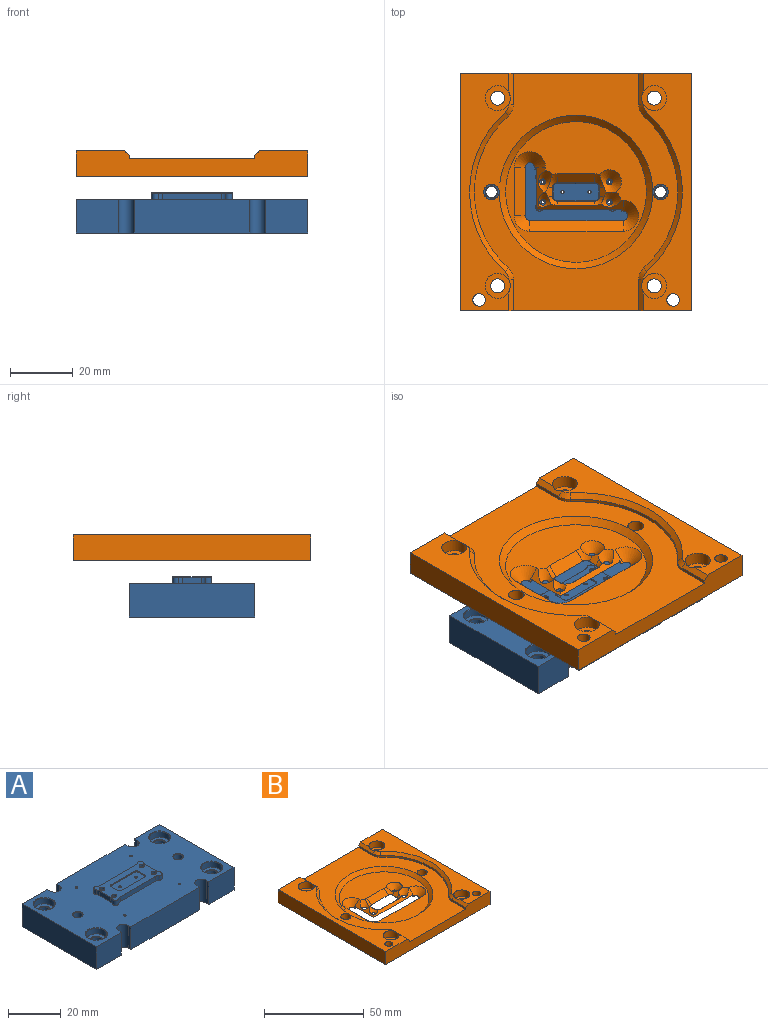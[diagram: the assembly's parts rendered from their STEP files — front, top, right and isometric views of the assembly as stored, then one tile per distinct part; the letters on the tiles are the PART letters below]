
ASSEMBLY  parts=2 mates=2
PART A: 211 faces, bbox 74x40x12.8 mm
  f0: plane 74x40mm, normal (0,0,-1), area 1926mm2, adj f20,f21,f22,f23,f24,f25,f26,f27
  f1: cylinder r=15mm len=15.84mm, axis (0,0,-1), area 30.9mm2, adj f61,f166,f171,f200
  f2: cylinder r=15mm len=15.14mm, axis (0,0,-1), area 29.4mm2, adj f61,f174,f175,f179
  f3: cylinder r=15mm len=18.2mm, axis (0,0,-1), area 36.2mm2, adj f61,f176,f177,f191
  f4: cylinder r=0.5mm len=1mm, axis (0,0,1), area 3.1mm2, adj f17,f158
  f5: cylinder r=0.5mm len=1mm, axis (0,0,1), area 3.1mm2, adj f16,f156
  f6: cylinder r=0.5mm len=1mm, axis (0,0,1), area 3.1mm2, adj f15,f154
  f7: cylinder r=0.5mm len=1mm, axis (0,0,1), area 3.1mm2, adj f14,f152
  f8: cylinder r=0.5mm len=1mm, axis (0,0,1), area 3.1mm2, adj f92,f150
  f9: cylinder r=0.5mm len=1mm, axis (0,0,1), area 3.1mm2, adj f92,f148
  f10: cylinder r=0.5mm len=1mm, axis (0,0,1), area 1.9mm2, adj f62,f145
  f11: cylinder r=0.5mm len=1mm, axis (0,0,1), area 1.9mm2, adj f62,f143
  f12: cylinder r=0.5mm len=1mm, axis (0,0,1), area 1.9mm2, adj f62,f141
  f13: cylinder r=0.5mm len=1mm, axis (0,0,1), area 1.9mm2, adj f62,f139
  f14: cone r=0mm half-angle=59deg, axis (0,0,1), area 2.7mm2, adj f7,f80
  f15: cone r=0mm half-angle=59deg, axis (0,0,1), area 2.7mm2, adj f6,f81
  f16: cone r=0mm half-angle=59deg, axis (0,0,1), area 2.7mm2, adj f5,f82
  f17: cone r=0mm half-angle=59deg, axis (0,0,1), area 2.7mm2, adj f4,f83
  f18: plane 25.7x12.2mm, normal (0,0,1), area 175.2mm2, adj f93,f94,f95,f96,f97,f98,f99,f100
  f19: cylinder r=0.3mm len=2.15mm, axis (0,0,1), area 0mm2, adj f62,f64,f77,f122
  f20: cylinder r=2.5mm len=10.6mm, axis (0,0,-1), area 83.3mm2, adj f0,f21,f44,f62
  f21: plane 10.6x1.5mm, normal (-1,0,0), area 15.9mm2, adj f0,f20,f22,f62
  f22: plane 13.5x10.6mm, normal (0,-1,0), area 143.1mm2, adj f0,f21,f23,f62
  f23: plane 40x10.6mm, normal (1,0,0), area 424mm2, adj f0,f22,f24,f62
  f24: plane 13.5x10.6mm, normal (0,1,0), area 143.1mm2, adj f0,f23,f25,f62
  f25: plane 10.6x1.5mm, normal (-1,0,0), area 15.9mm2, adj f0,f24,f26,f62
  f26: cylinder r=2.5mm len=10.6mm, axis (0,0,-1), area 83.3mm2, adj f0,f25,f27,f62
  f27: plane 10.6x1.5mm, normal (1,0,0), area 15.9mm2, adj f0,f26,f28,f62
  f28: plane 37x10.6mm, normal (0,1,0), area 392.2mm2, adj f0,f27,f29,f62
  f29: plane 10.6x1.5mm, normal (-1,0,0), area 15.9mm2, adj f0,f28,f30,f62
  f30: cylinder r=2.5mm len=10.6mm, axis (0,0,-1), area 83.3mm2, adj f0,f29,f31,f62
  f31: plane 10.6x1.5mm, normal (1,0,0), area 15.9mm2, adj f0,f30,f32,f62
  f32: plane 13.5x10.6mm, normal (0,1,0), area 143.1mm2, adj f0,f31,f33,f62
  f33: plane 40x10.6mm, normal (-1,0,0), area 424mm2, adj f0,f32,f34,f62
  f34: plane 13.5x10.6mm, normal (0,-1,0), area 143.1mm2, adj f0,f33,f35,f62
  f35: plane 10.6x1.5mm, normal (1,0,0), area 15.9mm2, adj f0,f34,f36,f62
  f36: cylinder r=2.5mm len=10.6mm, axis (0,0,-1), area 83.3mm2, adj f0,f35,f37,f62
  f37: plane 10.6x1.5mm, normal (-1,0,0), area 15.9mm2, adj f0,f36,f38,f62
  f38: plane 37x10.6mm, normal (0,-1,0), area 392.2mm2, adj f0,f37,f44,f62
  f39: cylinder r=4mm len=8mm, axis (0,0,-1), area 65.3mm2, adj f51,f135
  f40: cylinder r=1.8mm len=10.2mm, axis (0,0,-1), area 115.4mm2, adj f125,f134
  f41: cylinder r=1.8mm len=10.2mm, axis (0,0,-1), area 115.4mm2, adj f127,f133
  f42: cylinder r=4mm len=8mm, axis (0,0,-1), area 65.3mm2, adj f53,f136
  f43: cylinder r=4mm len=8mm, axis (0,0,-1), area 65.3mm2, adj f49,f138
  f44: plane 10.6x1.5mm, normal (1,0,0), area 15.9mm2, adj f0,f20,f38,f62
  f45: cylinder r=4mm len=8mm, axis (0,0,-1), area 65.3mm2, adj f47,f137
  f46: cylinder r=2.25mm len=7.4mm, axis (0,0,-1), area 104.6mm2, adj f126,f132
  f47: plane 8x8mm, normal (0,0,1), area 31.4mm2, adj f45,f132
  f48: cylinder r=2.25mm len=7.4mm, axis (0,0,-1), area 104.6mm2, adj f128,f131
  f49: plane 8x8mm, normal (0,0,1), area 31.4mm2, adj f43,f131
  f50: cylinder r=2.25mm len=7.4mm, axis (0,0,-1), area 104.6mm2, adj f124,f130
  f51: plane 8x8mm, normal (0,0,1), area 31.4mm2, adj f39,f130
  f52: cylinder r=2.25mm len=7.4mm, axis (0,0,-1), area 104.6mm2, adj f123,f129
  f53: plane 8x8mm, normal (0,0,1), area 31.4mm2, adj f42,f129
  f54: cone r=0mm half-angle=59deg, axis (0,0,-1), area 14.7mm2, adj f55
  f55: cylinder r=2mm len=4.85mm, axis (0,0,-1), area 60.9mm2, adj f54,f58
  f56: cone r=0mm half-angle=59deg, axis (0,0,-1), area 14.7mm2, adj f57
  f57: cylinder r=2mm len=4.85mm, axis (0,0,-1), area 60.9mm2, adj f56,f59
  f58: cone r=2mm half-angle=45deg, axis (0,0,-1), area 2.8mm2, adj f0,f55
  f59: cone r=2mm half-angle=45deg, axis (0,0,-1), area 2.8mm2, adj f0,f57
  f60: cylinder r=15mm len=18.2mm, axis (0,0,-1), area 36.2mm2, adj f61,f172,f173,f188
  f61: plane 33.6x30.2mm, normal (0,0,-1), area 728.5mm2, adj f1,f2,f3,f60,f159,f160,f161,f162
  f62: plane 74x40mm, normal (0,0,1), area 2368.6mm2, adj f10,f11,f12,f13,f19,f20,f21,f22
  f63: plane 6.04x2.15mm, normal (-1,0,0), area 13mm2, adj f62,f68,f73,f113
  f64: plane 19.05x2.15mm, normal (0,1,0), area 41mm2, adj f19,f62,f70,f121
  f65: plane 6.04x2.15mm, normal (1,0,0), area 13mm2, adj f62,f74,f79,f114
  f66: cylinder r=0.3mm len=2.15mm, axis (0,0,1), area 0mm2, adj f62,f67,f76,f106
  f67: plane 19.05x2.15mm, normal (0,-1,0), area 41mm2, adj f62,f66,f71,f105
  f68: cylinder r=2mm len=2.15mm, axis (0,0,1), area 2.7mm2, adj f62,f63,f69,f115
  f69: cylinder r=1.25mm len=2.15mm, axis (0,0,1), area 7.8mm2, adj f62,f68,f70,f117
  f70: cylinder r=2mm len=2.15mm, axis (0,0,1), area 3.1mm2, adj f62,f64,f69,f119
  f71: cylinder r=2mm len=2.15mm, axis (0,0,1), area 3.1mm2, adj f62,f67,f72,f107
  f72: cylinder r=1.25mm len=2.15mm, axis (0,0,1), area 7.8mm2, adj f62,f71,f73,f109
  f73: cylinder r=2mm len=2.15mm, axis (0,0,1), area 2.7mm2, adj f62,f63,f72,f111
  f74: cylinder r=2mm len=2.15mm, axis (0,0,1), area 2.7mm2, adj f62,f65,f75,f112
  f75: cylinder r=1.25mm len=2.15mm, axis (0,0,1), area 7.8mm2, adj f62,f74,f76,f110
  f76: cylinder r=2mm len=2.15mm, axis (0,0,1), area 3mm2, adj f62,f66,f75,f108
  f77: cylinder r=2mm len=2.15mm, axis (0,0,1), area 3mm2, adj f19,f62,f78,f120
  f78: cylinder r=1.25mm len=2.15mm, axis (0,0,1), area 7.8mm2, adj f62,f77,f79,f118
  f79: cylinder r=2mm len=2.15mm, axis (0,0,1), area 2.7mm2, adj f62,f65,f78,f116
  f80: cylinder r=1mm len=2mm, axis (0,0,1), area 6mm2, adj f14,f104
  f81: cylinder r=1mm len=2mm, axis (0,0,1), area 6mm2, adj f15,f103
  f82: cylinder r=1mm len=2mm, axis (0,0,1), area 6mm2, adj f16,f102
  f83: cylinder r=1mm len=2mm, axis (0,0,1), area 6mm2, adj f17,f101
  f84: plane 3.43x0.45mm, normal (-1,0,0), area 1.5mm2, adj f85,f91,f92,f95
  f85: cylinder r=1mm len=1mm, axis (0,0,1), area 0.7mm2, adj f84,f86,f92,f93
  f86: plane 12.43x0.45mm, normal (0,-1,0), area 5.6mm2, adj f85,f87,f92,f94
  f87: cylinder r=1mm len=1mm, axis (0,0,1), area 0.7mm2, adj f86,f88,f92,f96
  f88: plane 3.43x0.45mm, normal (1,0,0), area 1.5mm2, adj f87,f89,f92,f98
  f89: cylinder r=1mm len=1mm, axis (0,0,1), area 0.7mm2, adj f88,f90,f92,f100
  f90: plane 12.43x0.45mm, normal (0,1,0), area 5.6mm2, adj f89,f91,f92,f99
  f91: cylinder r=1mm len=1mm, axis (0,0,1), area 0.7mm2, adj f84,f90,f92,f97
  f92: plane 14.43x5.43mm, normal (0,0,1), area 75.8mm2, adj f8,f9,f84,f85,f86,f87,f88,f89
  f93: cone r=1mm half-angle=45deg, axis (0,0,1), area 0.1mm2, adj f18,f85,f94,f95
  f94: plane 12.43x0.05mm, normal (0,-0.71,0.71), area 0.9mm2, adj f18,f86,f93,f96
  f95: plane 3.43x0.05mm, normal (-0.71,0,0.71), area 0.2mm2, adj f18,f84,f93,f97
  f96: cone r=1mm half-angle=45deg, axis (0,0,1), area 0.1mm2, adj f18,f87,f94,f98
  f97: cone r=1mm half-angle=45deg, axis (0,0,1), area 0.1mm2, adj f18,f91,f95,f99
  f98: plane 3.43x0.05mm, normal (0.71,0,0.71), area 0.2mm2, adj f18,f88,f96,f100
  f99: plane 12.43x0.05mm, normal (0,0.71,0.71), area 0.9mm2, adj f18,f90,f97,f100
  f100: cone r=1mm half-angle=45deg, axis (0,0,1), area 0.1mm2, adj f18,f89,f98,f99
  f101: cone r=1mm half-angle=45deg, axis (0,0,1), area 0.5mm2, adj f18,f83
  f102: cone r=1mm half-angle=45deg, axis (0,0,1), area 0.5mm2, adj f18,f82
  f103: cone r=1mm half-angle=45deg, axis (0,0,1), area 0.5mm2, adj f18,f81
  f104: cone r=1mm half-angle=45deg, axis (0,0,1), area 0.5mm2, adj f18,f80
  f105: plane 19.05x0.05mm, normal (0,-0.71,0.71), area 1.3mm2, adj f18,f67,f106,f107
  f106: cone r=0.35mm half-angle=45deg, axis (0,0,1), area 0mm2, adj f18,f66,f105,f108
  f107: cone r=2mm half-angle=45deg, axis (0,0,1), area 0.1mm2, adj f18,f71,f105,f109
  f108: cone r=2mm half-angle=45deg, axis (0,0,1), area 0.1mm2, adj f18,f76,f106,f110
  f109: cone r=1.2mm half-angle=45deg, axis (0,0,-1), area 0.3mm2, adj f18,f72,f107,f111
  f110: cone r=1.2mm half-angle=45deg, axis (0,0,-1), area 0.3mm2, adj f18,f75,f108,f112
  f111: cone r=2mm half-angle=45deg, axis (0,0,1), area 0.1mm2, adj f18,f73,f109,f113
  f112: cone r=2mm half-angle=45deg, axis (0,0,1), area 0.1mm2, adj f18,f74,f110,f114
  f113: plane 6.04x0.05mm, normal (-0.71,0,0.71), area 0.4mm2, adj f18,f63,f111,f115
  f114: plane 6.04x0.05mm, normal (0.71,0,0.71), area 0.4mm2, adj f18,f65,f112,f116
  f115: cone r=2mm half-angle=45deg, axis (0,0,1), area 0.1mm2, adj f18,f68,f113,f117
  f116: cone r=2mm half-angle=45deg, axis (0,0,1), area 0.1mm2, adj f18,f79,f114,f118
  f117: cone r=1.2mm half-angle=45deg, axis (0,0,-1), area 0.3mm2, adj f18,f69,f115,f119
  f118: cone r=1.2mm half-angle=45deg, axis (0,0,-1), area 0.3mm2, adj f18,f78,f116,f120
  f119: cone r=2mm half-angle=45deg, axis (0,0,1), area 0.1mm2, adj f18,f70,f117,f121
  f120: cone r=2mm half-angle=45deg, axis (0,0,1), area 0.1mm2, adj f18,f77,f118,f122
  f121: plane 19.05x0.05mm, normal (0,0.71,0.71), area 1.3mm2, adj f18,f64,f119,f122
  f122: cone r=0.35mm half-angle=45deg, axis (0,0,1), area 0mm2, adj f18,f19,f120,f121
  f123: cone r=2.25mm half-angle=45deg, axis (0,0,-1), area 4.2mm2, adj f0,f52
  f124: cone r=2.25mm half-angle=45deg, axis (0,0,-1), area 4.2mm2, adj f0,f50
  f125: cone r=1.8mm half-angle=45deg, axis (0,0,-1), area 3.4mm2, adj f0,f40
  f126: cone r=2.25mm half-angle=45deg, axis (0,0,-1), area 4.2mm2, adj f0,f46
  f127: cone r=1.8mm half-angle=45deg, axis (0,0,-1), area 3.4mm2, adj f0,f41
  f128: cone r=2.25mm half-angle=45deg, axis (0,0,-1), area 4.2mm2, adj f0,f48
  f129: cone r=2.45mm half-angle=45deg, axis (0,0,1), area 4.2mm2, adj f52,f53
  f130: cone r=2.45mm half-angle=45deg, axis (0,0,1), area 4.2mm2, adj f50,f51
  f131: cone r=2.45mm half-angle=45deg, axis (0,0,1), area 4.2mm2, adj f48,f49
  f132: cone r=2.45mm half-angle=45deg, axis (0,0,1), area 4.2mm2, adj f46,f47
  f133: cone r=1.8mm half-angle=45deg, axis (0,0,1), area 3.4mm2, adj f41,f62
  f134: cone r=1.8mm half-angle=45deg, axis (0,0,1), area 3.4mm2, adj f40,f62
  f135: cone r=4mm half-angle=45deg, axis (0,0,1), area 7.3mm2, adj f39,f62
  f136: cone r=4mm half-angle=45deg, axis (0,0,1), area 7.3mm2, adj f42,f62
  f137: cone r=4mm half-angle=45deg, axis (0,0,1), area 7.3mm2, adj f45,f62
  f138: cone r=4mm half-angle=45deg, axis (0,0,1), area 7.3mm2, adj f43,f62
  f139: cone r=0mm half-angle=59deg, axis (0,0,-1), area 7.3mm2, adj f13,f140
  f140: cylinder r=1.5mm len=7.25mm, axis (0,0,-1), area 68.3mm2, adj f139,f203
  f141: cone r=0mm half-angle=59deg, axis (0,0,-1), area 7.3mm2, adj f12,f142
  f142: cylinder r=1.5mm len=7.25mm, axis (0,0,-1), area 68.3mm2, adj f141,f210
  f143: cone r=0mm half-angle=59deg, axis (0,0,-1), area 7.3mm2, adj f11,f144
  f144: cylinder r=1.5mm len=7.25mm, axis (0,0,-1), area 68.3mm2, adj f143,f201
  f145: cone r=0mm half-angle=59deg, axis (0,0,-1), area 7.3mm2, adj f10,f146
  f146: cylinder r=1.5mm len=7.25mm, axis (0,0,-1), area 68.3mm2, adj f145,f207
  f147: cylinder r=1.5mm len=8.55mm, axis (0,0,-1), area 80.6mm2, adj f148,f206
  f148: cone r=0mm half-angle=59deg, axis (0,0,-1), area 7.3mm2, adj f9,f147
  f149: cylinder r=1.5mm len=8.55mm, axis (0,0,-1), area 80.6mm2, adj f150,f205
  f150: cone r=0mm half-angle=59deg, axis (0,0,-1), area 7.3mm2, adj f8,f149
  f151: cylinder r=1.5mm len=7.75mm, axis (0,0,-1), area 73mm2, adj f152,f208
  f152: cone r=0mm half-angle=59deg, axis (0,0,-1), area 7.3mm2, adj f7,f151
  f153: cylinder r=1.5mm len=7.75mm, axis (0,0,-1), area 73mm2, adj f154,f209
  f154: cone r=0mm half-angle=59deg, axis (0,0,-1), area 7.3mm2, adj f6,f153
  f155: cylinder r=1.5mm len=7.75mm, axis (0,0,-1), area 73mm2, adj f156,f202
  f156: cone r=0mm half-angle=59deg, axis (0,0,-1), area 7.3mm2, adj f5,f155
  f157: cylinder r=1.5mm len=7.75mm, axis (0,0,-1), area 73mm2, adj f158,f204
  f158: cone r=0mm half-angle=59deg, axis (0,0,-1), area 7.3mm2, adj f4,f157
  f159: plane 2.94x2.6mm, normal (-0.66,-0.75,0), area 7.3mm2, adj f61,f161,f172,f192
  f160: plane 2.94x2.6mm, normal (0.66,0.75,0), area 7.3mm2, adj f61,f161,f171,f196
  f161: cylinder r=2.1mm len=3.67mm, axis (0,0,-1), area 12.2mm2, adj f61,f159,f160,f194
  f162: plane 2.94x2.6mm, normal (0.66,0.75,0), area 7.3mm2, adj f61,f164,f176,f187
  f163: plane 2.94x2.6mm, normal (-0.66,-0.75,0), area 7.3mm2, adj f61,f164,f175,f183
  f164: cylinder r=2.1mm len=3.67mm, axis (0,0,-1), area 12.2mm2, adj f61,f162,f163,f185
  f165: plane 2.94x2.6mm, normal (-0.66,0.75,0), area 7.3mm2, adj f61,f167,f177,f195
  f166: plane 3.57x3.16mm, normal (0.66,-0.75,0), area 8.8mm2, adj f1,f61,f167,f199
  f167: cylinder r=2.1mm len=3.67mm, axis (0,0,-1), area 12.2mm2, adj f61,f165,f166,f197
  f168: plane 2.94x2.6mm, normal (0.66,-0.75,0), area 7.3mm2, adj f61,f169,f173,f184
  f169: cylinder r=2.1mm len=3.67mm, axis (0,0,-1), area 12.2mm2, adj f61,f168,f170,f182
  f170: plane 2.94x2.6mm, normal (-0.66,0.75,0), area 7.3mm2, adj f61,f169,f174,f180
  f171: cylinder r=1mm len=1.85mm, axis (0,0,-1), area 2.5mm2, adj f1,f61,f160,f198
  f172: cylinder r=1mm len=1.85mm, axis (0,0,-1), area 2.5mm2, adj f60,f61,f159,f190
  f173: cylinder r=1mm len=1.85mm, axis (0,0,-1), area 2.5mm2, adj f60,f61,f168,f186
  f174: cylinder r=1mm len=1.85mm, axis (0,0,-1), area 2.5mm2, adj f2,f61,f170,f178
  f175: cylinder r=1mm len=1.85mm, axis (0,0,-1), area 2.5mm2, adj f2,f61,f163,f181
  f176: cylinder r=1mm len=1.85mm, axis (0,0,-1), area 2.5mm2, adj f3,f61,f162,f189
  f177: cylinder r=1mm len=1.85mm, axis (0,0,-1), area 2.5mm2, adj f3,f61,f165,f193
  f178: cone r=0.85mm half-angle=45deg, axis (0,0,1), area 0.3mm2, adj f0,f174,f179,f180
  f179: cone r=15.15mm half-angle=45deg, axis (0,0,-1), area 3.4mm2, adj f0,f2,f178,f181
  f180: plane 3.04x2.71mm, normal (-0.47,0.53,-0.71), area 0.8mm2, adj f0,f170,f178,f182
  f181: cone r=0.85mm half-angle=45deg, axis (0,0,1), area 0.3mm2, adj f0,f175,f179,f183
  f182: cone r=2.1mm half-angle=45deg, axis (0,0,-1), area 1.4mm2, adj f0,f169,f180,f184
  f183: plane 3.04x2.71mm, normal (-0.47,-0.53,-0.71), area 0.8mm2, adj f0,f163,f181,f185
  f184: plane 3.04x2.71mm, normal (0.47,-0.53,-0.71), area 0.8mm2, adj f0,f168,f182,f186
  f185: cone r=2.1mm half-angle=45deg, axis (0,0,-1), area 1.4mm2, adj f0,f164,f183,f187
  f186: cone r=0.85mm half-angle=45deg, axis (0,0,1), area 0.3mm2, adj f0,f173,f184,f188
  f187: plane 3.04x2.71mm, normal (0.47,0.53,-0.71), area 0.8mm2, adj f0,f162,f185,f189
  f188: cone r=15.15mm half-angle=45deg, axis (0,0,-1), area 4.2mm2, adj f0,f60,f186,f190
  f189: cone r=0.85mm half-angle=45deg, axis (0,0,1), area 0.3mm2, adj f0,f176,f187,f191
  f190: cone r=0.85mm half-angle=45deg, axis (0,0,1), area 0.3mm2, adj f0,f172,f188,f192
  f191: cone r=15.15mm half-angle=45deg, axis (0,0,-1), area 4.2mm2, adj f0,f3,f189,f193
  f192: plane 3.04x2.71mm, normal (-0.47,-0.53,-0.71), area 0.8mm2, adj f0,f159,f190,f194
  f193: cone r=0.85mm half-angle=45deg, axis (0,0,1), area 0.3mm2, adj f0,f177,f191,f195
  f194: cone r=2.1mm half-angle=45deg, axis (0,0,-1), area 1.4mm2, adj f0,f161,f192,f196
  f195: plane 3.04x2.71mm, normal (-0.47,0.53,-0.71), area 0.8mm2, adj f0,f165,f193,f197
  f196: plane 3.04x2.71mm, normal (0.47,0.53,-0.71), area 0.8mm2, adj f0,f160,f194,f198
  f197: cone r=2.1mm half-angle=45deg, axis (0,0,-1), area 1.4mm2, adj f0,f167,f195,f199
  f198: cone r=0.85mm half-angle=45deg, axis (0,0,1), area 0.3mm2, adj f0,f171,f196,f200
  f199: plane 3.67x3.19mm, normal (0.47,-0.53,-0.71), area 1mm2, adj f0,f166,f197,f200
  f200: cone r=15.15mm half-angle=45deg, axis (0,0,-1), area 3.5mm2, adj f0,f1,f198,f199
  f201: cone r=1.65mm half-angle=45deg, axis (0,0,-1), area 2.1mm2, adj f61,f144
  f202: cone r=1.5mm half-angle=45deg, axis (0,0,-1), area 2.1mm2, adj f61,f155
  f203: cone r=1.65mm half-angle=45deg, axis (0,0,-1), area 2.1mm2, adj f61,f140
  f204: cone r=1.5mm half-angle=45deg, axis (0,0,-1), area 2.1mm2, adj f61,f157
  f205: cone r=1.5mm half-angle=45deg, axis (0,0,-1), area 2.1mm2, adj f61,f149
  f206: cone r=1.5mm half-angle=45deg, axis (0,0,-1), area 2.1mm2, adj f61,f147
  f207: cone r=1.65mm half-angle=45deg, axis (0,0,-1), area 2.1mm2, adj f61,f146
  f208: cone r=1.5mm half-angle=45deg, axis (0,0,-1), area 2.1mm2, adj f61,f151
  f209: cone r=1.5mm half-angle=45deg, axis (0,0,-1), area 2.1mm2, adj f61,f153
  f210: cone r=1.65mm half-angle=45deg, axis (0,0,-1), area 2.1mm2, adj f61,f142
PART B: 95 faces, bbox 74.3x76.3x8.3 mm
  f0: cone r=1.5mm half-angle=45deg, axis (0,0,1), area 6.7mm2, adj f2,f13,f89,f90,f94
  f1: plane 13.41x3.51mm, normal (-0.71,0,0.71), area 23.2mm2, adj f2,f7,f20,f22,f72,f82,f87,f91
  f2: plane 28x3.8mm, normal (0,-0.71,0.71), area 49.1mm2, adj f0,f1,f3,f20,f22,f73,f82,f90
  f3: cone r=1.5mm half-angle=45deg, axis (0,0,1), area 50.5mm2, adj f2,f4,f20,f82
  f4: plane 29.8x3.5mm, normal (0,0.71,0.71), area 147.5mm2, adj f3,f5,f20,f82
  f5: cone r=1.5mm half-angle=45deg, axis (0,0,1), area 25.3mm2, adj f4,f6,f20,f82
  f6: plane 15.5x3.5mm, normal (0.71,0,0.71), area 76.7mm2, adj f5,f7,f20,f82
  f7: cone r=1.5mm half-angle=45deg, axis (0,0,1), area 50.5mm2, adj f1,f6,f20,f82
  f8: cylinder r=1mm len=2mm, axis (0,0,-1), area 0.3mm2, adj f22,f90
  f9: cylinder r=1mm len=2mm, axis (0,0,-1), area 0.3mm2, adj f22,f86
  f10: cylinder r=1mm len=2mm, axis (0,0,-1), area 0.3mm2, adj f22,f87
  f11: cylinder r=1mm len=2mm, axis (0,0,-1), area 0.3mm2, adj f22,f91
  f12: plane 3.03x0.05mm, normal (-1,0,0), area 0.2mm2, adj f13,f19,f22,f89
  f13: cylinder r=1.5mm len=1.5mm, axis (0,0,-1), area 0.1mm2, adj f0,f12,f14,f22
  f14: plane 12.03x0.05mm, normal (0,1,0), area 0.6mm2, adj f13,f15,f22,f94
  f15: cylinder r=1.5mm len=1.5mm, axis (0,0,-1), area 0.1mm2, adj f14,f16,f22,f93
  f16: plane 3.03x0.05mm, normal (1,0,0), area 0.2mm2, adj f15,f17,f22,f92
  f17: cylinder r=1.5mm len=1.5mm, axis (0,0,-1), area 0.1mm2, adj f16,f18,f22,f88
  f18: plane 12.03x0.05mm, normal (0,-1,0), area 0.6mm2, adj f17,f19,f22,f84
  f19: cylinder r=1.5mm len=1.5mm, axis (0,0,-1), area 0.1mm2, adj f12,f18,f22,f85
  f20: plane 76x74mm, normal (0,0,-1), area 4900.1mm2, adj f1,f2,f3,f4,f5,f6,f7,f23
  f21: plane 76x65mm, normal (0,0,1), area 2011.2mm2, adj f23,f24,f31,f32,f37,f38,f39,f40
  f22: plane 27.2x12.9mm, normal (0,0,-1), area 229.7mm2, adj f1,f2,f8,f9,f10,f11,f12,f13
  f23: cylinder r=2.5mm len=5.5mm, axis (0,0,-1), area 86.4mm2, adj f20,f21
  f24: cylinder r=2.5mm len=5.5mm, axis (0,0,-1), area 172.8mm2, adj f20,f21
  f25: plane 76x8mm, normal (1,0,0), area 608mm2, adj f20,f31,f32,f33
  f26: plane 76x8mm, normal (-1,0,0), area 608mm2, adj f20,f31,f32,f36
  f27: cylinder r=2.25mm len=4.5mm, axis (0,0,-1), area 56.5mm2, adj f20,f50
  f28: cylinder r=2.25mm len=4.5mm, axis (0,0,-1), area 56.5mm2, adj f20,f48
  f29: cylinder r=2.25mm len=4.5mm, axis (0,0,-1), area 56.5mm2, adj f20,f46
  f30: cylinder r=2.25mm len=4.5mm, axis (0,0,-1), area 56.5mm2, adj f20,f44
  f31: plane 74x8mm, normal (0,-1,0), area 489.7mm2, adj f20,f21,f25,f26,f33,f36,f39,f40
  f32: plane 74x8mm, normal (0,1,0), area 489.7mm2, adj f20,f21,f25,f26,f33,f36,f37,f42
  f33: plane 76x15.5mm, normal (0,0,1), area 608.7mm2, adj f25,f31,f32,f35,f47,f49,f55,f56
  f34: cylinder r=2mm len=8mm, axis (0,0,-1), area 100.5mm2, adj f20,f36
  f35: cylinder r=2mm len=8mm, axis (0,0,-1), area 100.5mm2, adj f20,f33
  f36: plane 76x15.5mm, normal (0,0,1), area 608.7mm2, adj f26,f31,f32,f34,f43,f45,f60,f61
  f37: plane 10.05x1mm, normal (1,0,0), area 10mm2, adj f21,f32,f51,f64
  f38: cylinder r=32.5mm len=48.45mm, axis (0,0,1), area 54.7mm2, adj f21,f51,f52,f62
  f39: plane 10.05x1mm, normal (1,0,0), area 10mm2, adj f21,f31,f52,f60
  f40: plane 10.05x1mm, normal (-1,0,0), area 10mm2, adj f21,f31,f53,f59
  f41: cylinder r=32.5mm len=48.45mm, axis (0,0,1), area 54.7mm2, adj f21,f53,f54,f57
  f42: plane 10.05x1mm, normal (-1,0,0), area 10mm2, adj f21,f32,f54,f55
  f43: cylinder r=4mm len=8mm, axis (0,0,1), area 99.5mm2, adj f36,f44,f64
  f44: plane 8x8mm, normal (0,0,1), area 34.4mm2, adj f30,f43
  f45: cylinder r=4mm len=8mm, axis (0,0,1), area 99.5mm2, adj f36,f46,f60
  f46: plane 8x8mm, normal (0,0,1), area 34.4mm2, adj f29,f45
  f47: cylinder r=4mm len=8mm, axis (0,0,1), area 99.2mm2, adj f33,f48,f59
  f48: plane 8x8mm, normal (0,0,1), area 34.4mm2, adj f28,f47
  f49: cylinder r=4mm len=8mm, axis (0,0,1), area 99.2mm2, adj f33,f50,f55
  f50: plane 8x8mm, normal (0,0,1), area 34.4mm2, adj f27,f49
  f51: cylinder r=5mm len=3.73mm, axis (0,0,1), area 4.2mm2, adj f21,f37,f38,f63
  f52: cylinder r=5mm len=3.73mm, axis (0,0,1), area 4.2mm2, adj f21,f38,f39,f61
  f53: cylinder r=5mm len=3.73mm, axis (0,0,1), area 4.2mm2, adj f21,f40,f41,f58
  f54: cylinder r=5mm len=3.73mm, axis (0,0,1), area 4.2mm2, adj f21,f41,f42,f56
  f55: plane 10.05x1.5mm, normal (-0.71,0,0.71), area 19.5mm2, adj f32,f33,f42,f49,f56
  f56: cone r=3.5mm half-angle=45deg, axis (0,0,-1), area 7.6mm2, adj f33,f54,f55,f57
  f57: cone r=32.5mm half-angle=45deg, axis (0,0,1), area 118.6mm2, adj f33,f41,f56,f58
  f58: cone r=5mm half-angle=45deg, axis (0,0,-1), area 7.6mm2, adj f33,f53,f57,f59
  f59: plane 10.05x1.5mm, normal (-0.71,0,0.71), area 19.5mm2, adj f31,f33,f40,f47,f58
  f60: plane 10.3x1.75mm, normal (0.71,0,0.71), area 19.5mm2, adj f31,f36,f39,f45,f61
  f61: cone r=5mm half-angle=45deg, axis (0,0,-1), area 7.6mm2, adj f36,f52,f60,f62
  f62: cone r=32.5mm half-angle=45deg, axis (0,0,1), area 118.6mm2, adj f36,f38,f61,f63
  f63: cone r=5mm half-angle=45deg, axis (0,0,-1), area 7.6mm2, adj f36,f51,f62,f64
  f64: plane 10.3x1.75mm, normal (0.71,0,0.71), area 19.5mm2, adj f32,f36,f37,f43,f63
  f65: cylinder r=1mm len=0.6mm, axis (0,0,1), area 0.4mm2, adj f20,f22,f66,f73
  f66: plane 7.2x0.6mm, normal (-1,0,0), area 4.3mm2, adj f20,f22,f65,f67
  f67: cylinder r=1mm len=0.6mm, axis (0,0,1), area 0.4mm2, adj f20,f22,f66,f68
  f68: cylinder r=2mm len=3.2mm, axis (0,0,1), area 3.4mm2, adj f20,f22,f67,f69
  f69: cylinder r=1mm len=0.6mm, axis (0,0,1), area 0.4mm2, adj f20,f22,f68,f70
  f70: plane 21.5x0.6mm, normal (0,-1,0), area 12.9mm2, adj f20,f22,f69,f71
  f71: cylinder r=1mm len=0.6mm, axis (0,0,1), area 0.4mm2, adj f20,f22,f70,f72
  f72: cylinder r=2mm len=1.9mm, axis (0,0,1), area 1mm2, adj f1,f20,f22,f71
  f73: cylinder r=2mm len=1.9mm, axis (0,0,1), area 1mm2, adj f2,f20,f22,f65
  f74: cone r=0mm half-angle=59deg, axis (0,0,-1), area 22.9mm2, adj f75
  f75: cylinder r=2.5mm len=5mm, axis (0,0,-1), area 31.4mm2, adj f20,f74
  f76: cone r=0mm half-angle=59deg, axis (0,0,-1), area 22.9mm2, adj f77
  f77: cylinder r=2.5mm len=5mm, axis (0,0,-1), area 31.4mm2, adj f20,f76
  f78: cone r=0mm half-angle=59deg, axis (0,0,-1), area 22.9mm2, adj f79
  f79: cylinder r=2.5mm len=5mm, axis (0,0,-1), area 31.4mm2, adj f20,f78
  f80: cone r=0mm half-angle=59deg, axis (0,0,-1), area 22.9mm2, adj f81
  f81: cylinder r=2.5mm len=5mm, axis (0,0,-1), area 31.4mm2, adj f20,f80
  f82: plane 45x45mm, normal (0,0,1), area 857.5mm2, adj f1,f2,f3,f4,f5,f6,f7,f83
  f83: cone r=22.5mm half-angle=45deg, axis (0,0,1), area 417.6mm2, adj f21,f82
  f84: plane 12.03x2.85mm, normal (0,-0.71,0.71), area 48.5mm2, adj f18,f82,f85,f88
  f85: cone r=1.5mm half-angle=45deg, axis (0,0,1), area 10.6mm2, adj f19,f82,f84,f86,f89
  f86: cone r=1mm half-angle=45deg, axis (0,0,1), area 48.8mm2, adj f9,f82,f85,f89,f90
  f87: cone r=1mm half-angle=45deg, axis (0,0,1), area 24.7mm2, adj f1,f10,f82,f88,f91,f92
  f88: cone r=1.5mm half-angle=45deg, axis (0,0,1), area 10.6mm2, adj f17,f82,f84,f87,f92
  f89: plane 3.28x2.6mm, normal (-0.71,0,0.71), area 7.9mm2, adj f0,f12,f85,f86,f90
  f90: cone r=1mm half-angle=45deg, axis (0,0,1), area 27.8mm2, adj f0,f2,f8,f82,f86,f89
  f91: cone r=1mm half-angle=45deg, axis (0,0,1), area 14.9mm2, adj f1,f2,f11,f87,f92,f93
  f92: plane 3.28x2.6mm, normal (0.71,0,0.71), area 7.9mm2, adj f16,f87,f88,f91,f93
  f93: cone r=1.5mm half-angle=45deg, axis (0,0,1), area 6.7mm2, adj f2,f15,f91,f92,f94
  f94: plane 12.03x1.22mm, normal (0,0.71,0.71), area 20.7mm2, adj f0,f2,f14,f93
PLACE A at identity
PLACE B t=(0,0,18.2)mm
MATE parallel B.f20 <-> A.f0  axis (0,0,-1) through (0.1,0.28,18.2)mm
MATE slider A.f41 <-> B.f24  axis (0,0,-1) through (-27,0,0)mm
